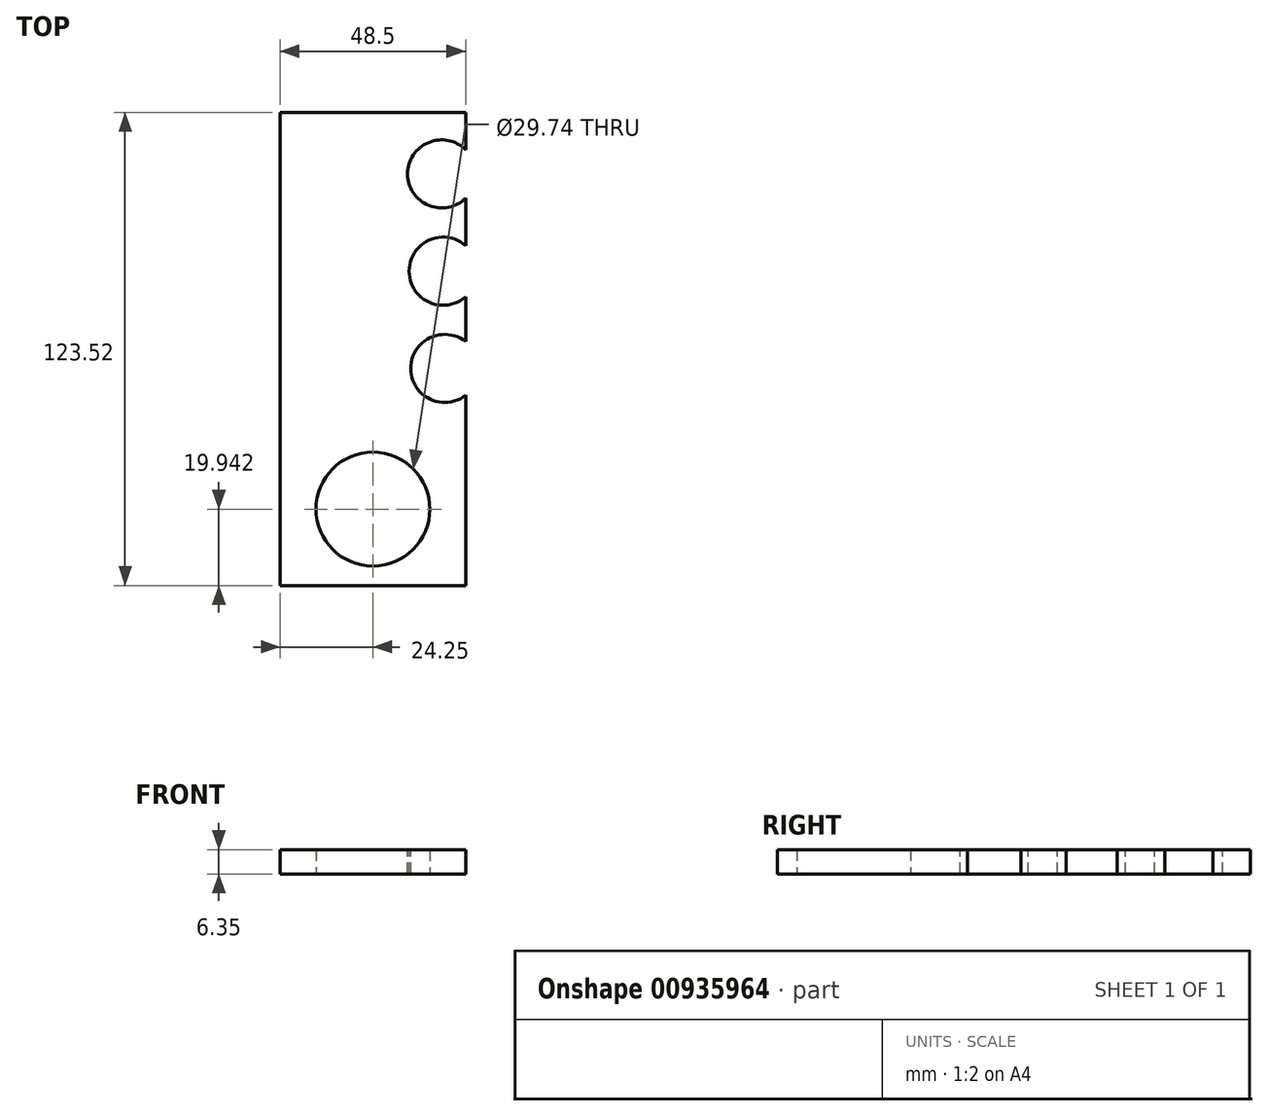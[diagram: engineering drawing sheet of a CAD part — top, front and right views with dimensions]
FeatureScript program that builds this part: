
annotation { "Feature Type Name" : "Feature", "Feature Type Description" : "" }
export const myFeature = defineFeature(function(context is Context, id is Id, definition is map)
    precondition{}
    {
        {
            var Q0;
            Q0=qCreatedBy(makeId("Top.planeOp"),FACE);
            var sketch = newSketch(context, id + "F0", { "sketchPlane" : qUnion([Q0])});
            skLineSegment(sketch, "E0.bottom", {"start": v(24.25, -61.76) * mm, "end": v(-24.25, -61.76) * mm});
            skLineSegment(sketch, "E0.top", {"start": v(24.25, 61.76) * mm, "end": v(-24.25, 61.76) * mm});
            skLineSegment(sketch, "E0.left", {"start": v(24.25, -61.76) * mm, "end": v(24.25, 61.76) * mm});
            skLineSegment(sketch, "E0.right", {"start": v(-24.25, -61.76) * mm, "end": v(-24.25, 61.76) * mm});
            skPoint(sketch, "E0.middle", {"position": v(0, 0) * mm});
            skCircle(sketch, "E1", {"center": v(0, -41.82) * mm, "radius": 14.87 * mm});
            skSolve(sketch);
        }
        {
            var Q0;
            Q0 = qSketchRegion(id + "F0", true);
            extrude(context, id + "F1", {"entities" : qUnion([Q0]), "depth" : 6.35 * mm, "offsetDistance" : 25.4 * mm});
        }
        {
            var Q0;
            Q0=makeQuery(id+"F1.opExtrude","CAP_FACE",FACE,{"disambiguationData":[OSD([sQuery(id+"F0.wireOp",EDGE,"E0.bottom"),sQuery(id+"F0.wireOp",EDGE,"E0.top"),sQuery(id+"F0.wireOp",EDGE,"E0.left"),sQuery(id+"F0.wireOp",EDGE,"E0.right"),sQuery(id+"F0.wireOp",EDGE,"E1")])],"isStart":false});
            var sketch = newSketch(context, id + "F2", { "sketchPlane" : qUnion([Q0])});
            skCircle(sketch, "E2", {"center": v(17.95, 45.7) * mm, "radius": 8.9 * mm});
            skCircle(sketch, "E3.1.0.0", {"center": v(18.35, 20.3) * mm, "radius": 8.9 * mm});
            skCircle(sketch, "E3.2.0.0", {"center": v(18.75, -5.09) * mm, "radius": 8.9 * mm});
            skLineSegment(sketch, "E3.direction1", {"start": v(17.95, 45.7) * mm, "end": v(18.35, 20.3) * mm, "construction": true});
            skSolve(sketch);
        }
        {
            var Q0;
            Q0 = qSketchRegion(id + "F2", true);
            extrude(context, id + "F3", {"entities" : qUnion([Q0]), "operationType" : NewBodyOperationType.REMOVE, "endBound" : BoundingType.THROUGH_ALL, "oppositeDirection" : true, "depth" : 25.4 * mm, "offsetDistance" : 25.4 * mm});
        }
    });
